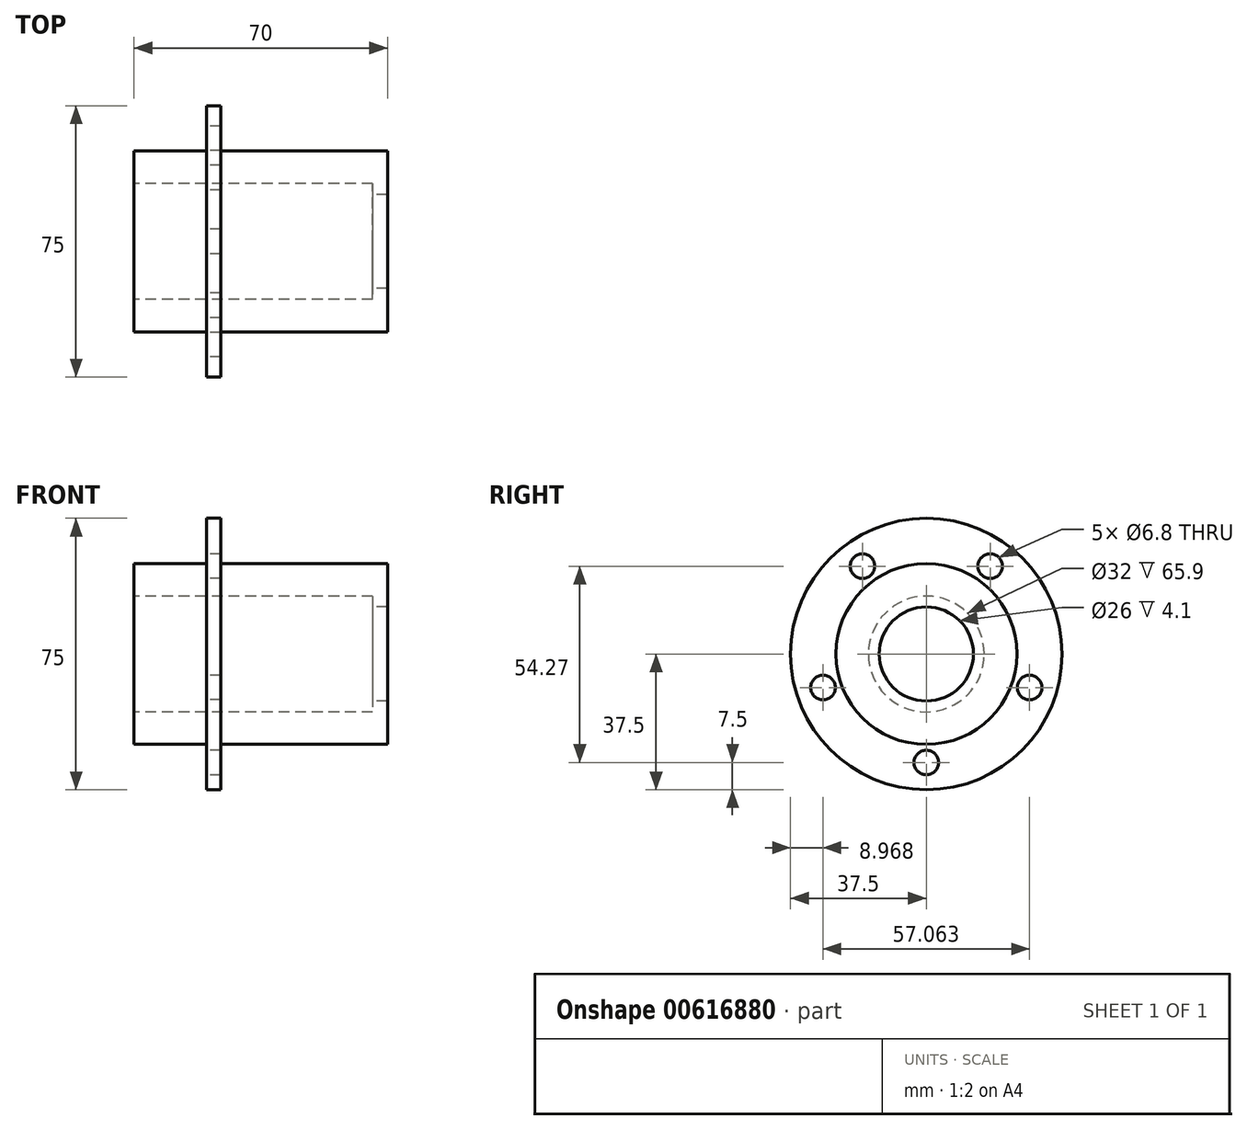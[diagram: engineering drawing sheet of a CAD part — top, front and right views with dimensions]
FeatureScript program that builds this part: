
annotation { "Feature Type Name" : "Feature", "Feature Type Description" : "" }
export const myFeature = defineFeature(function(context is Context, id is Id, definition is map)
    precondition{}
    {
        {
            var Q0;
            Q0=qCreatedBy(makeId("Front.planeOp"),FACE);
            var sketch = newSketch(context, id + "F0", { "sketchPlane" : qUnion([Q0])});
            skLineSegment(sketch, "E0", {"start": v(0, 37.5) * mm, "end": v(4, 37.5) * mm});
            skLineSegment(sketch, "E1", {"start": v(4, 37.5) * mm, "end": v(4, 25) * mm});
            skLineSegment(sketch, "E2", {"start": v(4, 25) * mm, "end": v(50, 25) * mm});
            skLineSegment(sketch, "E3", {"start": v(50, 25) * mm, "end": v(50, 13) * mm});
            skLineSegment(sketch, "E4", {"start": v(50, 13) * mm, "end": v(45.9, 13) * mm});
            skLineSegment(sketch, "E5", {"start": v(45.9, 13) * mm, "end": v(45.9, 16) * mm});
            skLineSegment(sketch, "E6", {"start": v(45.9, 16) * mm, "end": v(-20, 16) * mm});
            skLineSegment(sketch, "E7", {"start": v(-20, 16) * mm, "end": v(-20, 25) * mm});
            skLineSegment(sketch, "E8", {"start": v(-20, 25) * mm, "end": v(0, 25) * mm});
            skLineSegment(sketch, "E9", {"start": v(0, 25) * mm, "end": v(0, 37.5) * mm});
            skLineSegment(sketch, "E10", {"start": v(0, 0) * mm, "end": v(80.55, 0) * mm, "construction": true});
            skSolve(sketch);
        }
        {
            var Q0;
            Q0 = qSketchRegion(id + "F0", true);
            var Q1;
            Q1 = qConstructionFilter(qBodyType(qCreatedBy(id + "F0" ,EDGE), BodyType.WIRE), ConstructionObject.NO);
            var Q2;
            Q2=sQuery(id+"F0.wireOp",EDGE,"E10");
            revolve(context, id + "F1", {"surfaceOperationType" : NewSurfaceOperationType.NEW, "entities" : qUnion([Q0]), "surfaceEntities" : qUnion([Q1]), "axis" : qUnion([Q2]), "revolveType" : RevolveType.FULL});
        }
        {
            var Q0;
            Q0=makeQuery(id+"F1.opRevolve","SWEPT_FACE",FACE,{"disambiguationData":[OSD([sQuery(id+"F0.wireOp",EDGE,"E1")])]});
            var sketch = newSketch(context, id + "F2", { "sketchPlane" : qUnion([Q0])});
            skPoint(sketch, "E11", {"position": v(0, -30) * mm});
            skPoint(sketch, "E12.1.0", {"position": v(28.53, -9.27) * mm});
            skPoint(sketch, "E12.2.0", {"position": v(17.63, 24.27) * mm});
            skPoint(sketch, "E12.3.0", {"position": v(-17.63, 24.27) * mm});
            skPoint(sketch, "E12.4.0", {"position": v(-28.53, -9.27) * mm});
            skPoint(sketch, "E12.center", {"position": v(0, 0) * mm});
            skSolve(sketch);
        }
        {
            var Q0;
            Q0=sQuery(id+"F2.wireOp",VERTEX,"E11");
            var Q1;
            Q1=sQuery(id+"F2.wireOp",VERTEX,"E12.4.0");
            var Q2;
            Q2=sQuery(id+"F2.wireOp",VERTEX,"E12.2.0");
            var Q3;
            Q3=sQuery(id+"F2.wireOp",VERTEX,"E12.3.0");
            var Q4;
            Q4=sQuery(id+"F2.wireOp",VERTEX,"E12.1.0");
            var Q5;
            Q5=makeQuery(id+"F1.opRevolve","SWEPT_BODY",BODY,{"disambiguationData":[OSD([sQuery(id+"F0.wireOp",EDGE,"E0"),sQuery(id+"F0.wireOp",EDGE,"E1"),sQuery(id+"F0.wireOp",EDGE,"E2"),sQuery(id+"F0.wireOp",EDGE,"E3"),sQuery(id+"F0.wireOp",EDGE,"E4"),sQuery(id+"F0.wireOp",EDGE,"E5"),sQuery(id+"F0.wireOp",EDGE,"E6"),sQuery(id+"F0.wireOp",EDGE,"E7"),sQuery(id+"F0.wireOp",EDGE,"E8"),sQuery(id+"F0.wireOp",EDGE,"E9")])]});
            hole(context, id + "F3", {"style" : HoleStyle.SIMPLE, "endStyle" : HoleEndStyle.BLIND, "standardTappedOrClearance" : lookupTablePath({ "standard" : "ISO", "engagement" : "75%", "pitch" : "1.25 mm", "size" : "M8", "type" : "Tapped" }), "standardBlindInLast" : lookupTablePath({ "standard" : "ISO", "engagement" : "75%", "pitch" : "1.25 mm", "size" : "M8", "type" : "Tapped" }), "holeDiameter" : 6.8 * mm, "majorDiameter" : 8 * mm, "showTappedDepth" : true, "holeDepth" : 48.75 * mm, "isTappedThrough" : true, "tappedDepth" : 45 * mm, "tapClearance" : 3, "locations" : qUnion([Q0, Q1, Q2, Q3, Q4]), "scope" : qUnion([Q5]), "startStyle" : HoleStartStyle.PART});
        }
    });
